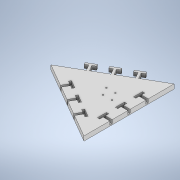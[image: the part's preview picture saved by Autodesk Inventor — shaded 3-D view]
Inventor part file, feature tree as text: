
AUTODESK INVENTOR PART (.ipt)
format: ipt  version: 2022.3 (Build 263350000, 350)  size: 414,208 bytes
history: native  units: mm
features: extrude x6, thicken_offset x6, sketch x4, hole x1, projected_geometry x1
ambient origin geometry x8: Origin, YZ Plane, XZ Plane, XY Plane, X Axis, Y Axis, Z Axis, Center Point
bodies: Solid1 (feature_tree)
feature tree (18):
  sketch  "Sketch1"  dims[d1=200.0mm d2=35.0mm]
  extrude  "Extrusion1"  Depth=35.0mm
  extrude  "Extrusion2"  Depth=5.0mm
  extrude  "Extrusion3"  Depth=40.0mm
  extrude  "Extrusion4"  Depth=10.0mm TaperAngle=0.0deg
  sketch  "Sketch3"  dims[d5=20.0mm d6=30.0mm d8=40.0mm d9=30.0mm d11=40.0mm]
  extrude  "Extrusion6"  Depth=2.2mm TaperAngle=0.0deg
  extrude  "Extrusion7"  Depth=22.0mm
  hole  "Hole1"  [1 undecoded]
  thicken_offset  "Thicken1"
  thicken_offset  "Thicken2"
  thicken_offset  "Thicken3"
  thicken_offset  "Thicken4"
  thicken_offset  "Thicken5"
  thicken_offset  "Thicken6"
  sketch  "Sketch2"  dims[d3=5.0mm d4=5.0mm]
  projected_geometry  "Projected Loop1"
  sketch  "Sketch4"  dims[d14=10.0mm d15=0.0mm d16=10.0mm d17=0.0mm d18=2.2mm d19=0.0mm d20=22.0mm d21=3.0mm d22=1.5mm d23=0.0mm d24=15.0mm d25=120.0deg d26=10.0mm d27=5.0mm d28=20.0mm d29=90.0deg d30=5.0mm d31=2.5mm d32=5.0mm d33=20.0mm d35=120.0deg d37=30.0mm d39=40.0mm d40=30.0mm d42=40.0mm d45=30.0mm d47=40.0mm d48=30.0mm d50=40.0mm d55=7.8mm d56=0.0mm d57=10.0mm d58=0.0mm d59=40.0mm d60=2.2mm d61=6.0mm d62=3.1mm d63=4.1mm d64=90.0deg d65=2.2mm d66=0.0mm d67=0.05mm d68=0.05mm d69=0.05mm d70=0.05mm d71=0.05mm d72=0.05mm d73=0.05mm d74=0.05mm d75=0.05mm d76=0.05mm d77=0.05mm d78=0.05mm]
note: 1 required parameter value undecoded (feature->parameter linkage not recoverable at this tier; creation-order binding heuristic only, values carry confidence <= 0.55)
